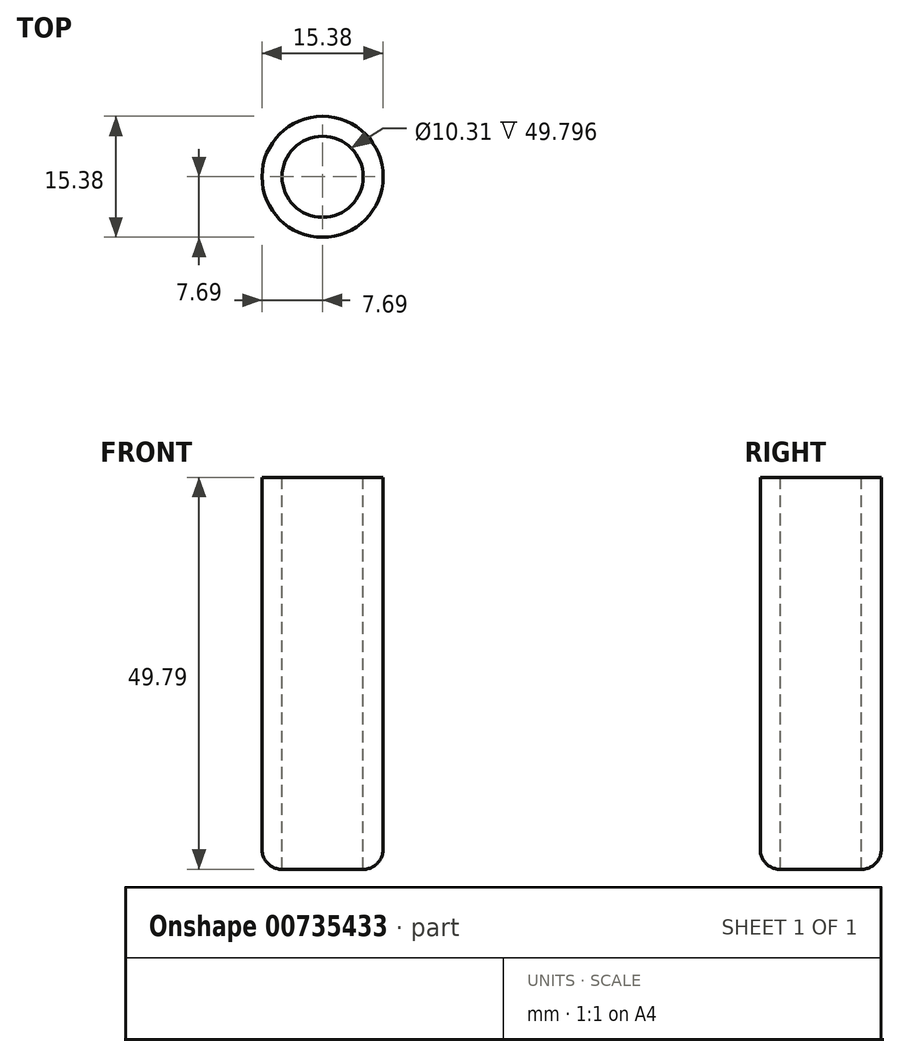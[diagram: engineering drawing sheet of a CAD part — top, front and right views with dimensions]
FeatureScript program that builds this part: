
annotation { "Feature Type Name" : "Feature", "Feature Type Description" : "" }
export const myFeature = defineFeature(function(context is Context, id is Id, definition is map)
    precondition{}
    {
        {
            var Q0;
            Q0=qCreatedBy(makeId("Front.planeOp"),FACE);
            var sketch = newSketch(context, id + "F0", { "sketchPlane" : qUnion([Q0])});
            skLineSegment(sketch, "E0.bottom", {"start": v(0, 29.23) * mm, "end": v(7.7, 29.23) * mm});
            skLineSegment(sketch, "E0.top", {"start": v(0, -20.56) * mm, "end": v(7.7, -20.56) * mm});
            skLineSegment(sketch, "E0.left", {"start": v(0, 29.23) * mm, "end": v(0, -20.56) * mm});
            skLineSegment(sketch, "E0.right", {"start": v(7.7, 29.23) * mm, "end": v(7.7, -20.56) * mm});
            skSolve(sketch);
        }
        {
            var Q0;
            Q0=makeQuery(id+"F0.imprint","IMPRINT",FACE,{"disambiguationData":[TD([[makeQuery(id+"F0.imprint","IMPRINT",EDGE,{"derivedFrom":sQuery(id+"F0.wireOp",EDGE,"E0.bottom")}),-1.0]])]});
            var Q1;
            Q1=sQuery(id+"F0.wireOp",EDGE,"E0.left");
            revolve(context, id + "F1", {"surfaceOperationType" : NewSurfaceOperationType.NEW, "entities" : qUnion([Q0]), "axis" : qUnion([Q1]), "revolveType" : RevolveType.FULL});
        }
        {
            var Q0;
            Q0=makeQuery(id+"F1.opRevolve","SWEPT_FACE",FACE,{"disambiguationData":[OSD([sQuery(id+"F0.wireOp",EDGE,"E0.bottom")])]});
            var Q1;
            Q1=makeQuery(id+"F1.opRevolve","SWEPT_FACE",FACE,{"disambiguationData":[OSD([sQuery(id+"F0.wireOp",EDGE,"E0.top")])]});
            var Q2;
            Q2=makeQuery(id+"F1.opRevolve","SWEPT_BODY",BODY,{"disambiguationData":[OSD([sQuery(id+"F0.wireOp",EDGE,"E0.bottom"),sQuery(id+"F0.wireOp",EDGE,"E0.top"),sQuery(id+"F0.wireOp",EDGE,"E0.left"),sQuery(id+"F0.wireOp",EDGE,"E0.right")])]});
            shell(context, id + "F2", {"entities" : qUnion([Q0, Q1]), "parts" : qUnion([Q2]), "thickness" : 2.54 * mm});
        }
        {
            var Q0;
            Q0=makeQuery(id+"F1.opRevolve","SWEPT_EDGE",EDGE,{"disambiguationData":[OSD([sQuery(id+"F0.wireOp",EDGE,"E0.top"),sQuery(id+"F0.wireOp",EDGE,"E0.right")])]});
            fillet(context, id + "F3", {"entities" : qUnion([Q0]), "radius" : 2.54 * mm, "tangentPropagation" : true, "allowEdgeOverflow" : false});
        }
    });
